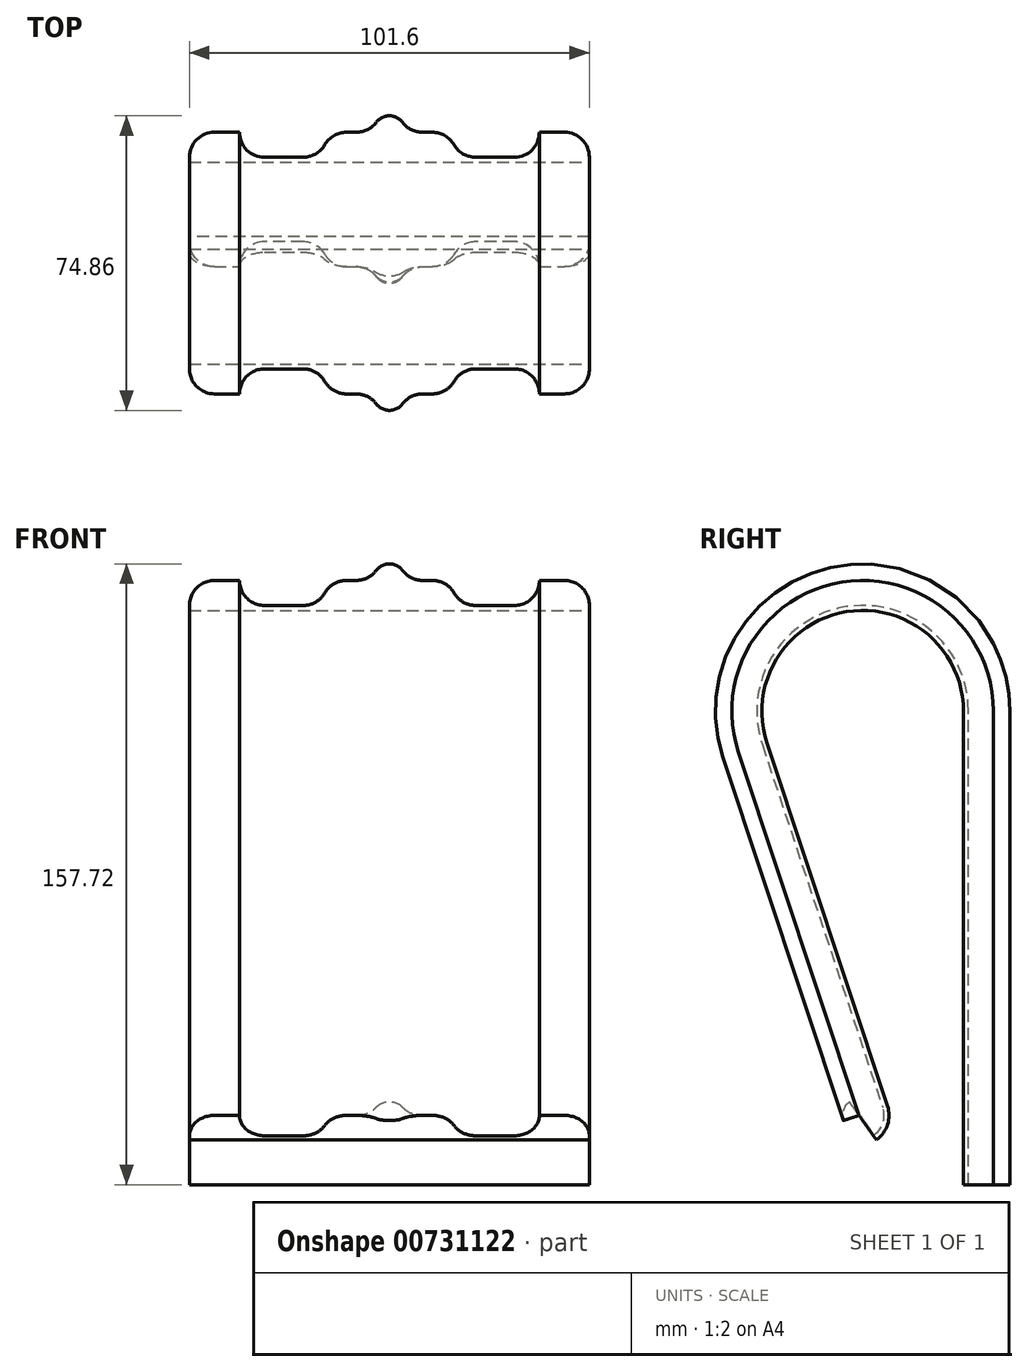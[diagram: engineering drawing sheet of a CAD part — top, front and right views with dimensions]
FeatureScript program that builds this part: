
annotation { "Feature Type Name" : "Feature", "Feature Type Description" : "" }
export const myFeature = defineFeature(function(context is Context, id is Id, definition is map)
    precondition{}
    {
        {
            var Q0;
            Q0=qCreatedBy(makeId("Front.planeOp"),FACE);
            var sketch = newSketch(context, id + "F0", { "sketchPlane" : qUnion([Q0])});
            skLineSegment(sketch, "E0.bottom", {"start": v(-50.8, 0) * mm, "end": v(50.8, 0) * mm});
            skLineSegment(sketch, "E0.top", {"start": v(-44.45, 7.62) * mm, "end": v(-38.1, 7.62) * mm});
            skLineSegment(sketch, "E0.left", {"start": v(-50.8, 0) * mm, "end": v(-50.8, 1.27) * mm});
            skLineSegment(sketch, "E0.right", {"start": v(50.8, 0) * mm, "end": v(50.8, 1.27) * mm});
            skLineSegment(sketch, "E1", {"start": v(-38.1, 7.62) * mm, "end": v(-38.1, 7.62) * mm});
            skLineSegment(sketch, "E2", {"start": v(-31.75, 1.27) * mm, "end": v(-21.93, 1.27) * mm});
            skLineSegment(sketch, "E3", {"start": v(-15.58, 7.62) * mm, "end": v(-15.58, 7.62) * mm});
            skArc(sketch, "E4", {"start": v(3.35, 10.15) * mm, "mid": v(0, 11.82) * mm, "end": v(-3.35, 10.15) * mm});
            skLineSegment(sketch, "E5", {"start": v(15.58, 7.62) * mm, "end": v(15.58, 7.62) * mm});
            skLineSegment(sketch, "E6", {"start": v(21.93, 1.27) * mm, "end": v(31.75, 1.27) * mm});
            skLineSegment(sketch, "E7", {"start": v(38.1, 7.62) * mm, "end": v(38.1, 7.62) * mm});
            skPoint(sketch, "E8.visualSharp", {"position": v(-50.8, 7.62) * mm});
            skArc(sketch, "E8.filletArc", {"start": v(-44.45, 7.62) * mm, "mid": v(-48.94, 5.76) * mm, "end": v(-50.8, 1.27) * mm});
            skPoint(sketch, "E9.visualSharp", {"position": v(-38.1, 1.27) * mm});
            skArc(sketch, "E9.filletArc", {"start": v(-38.1, 7.62) * mm, "mid": v(-36.24, 3.13) * mm, "end": v(-31.75, 1.27) * mm});
            skPoint(sketch, "E10.visualSharp", {"position": v(-15.58, 1.27) * mm});
            skArc(sketch, "E10.filletArc", {"start": v(-21.93, 1.27) * mm, "mid": v(-18.75, 2.12) * mm, "end": v(-16.43, 4.45) * mm});
            skPoint(sketch, "E11.visualSharp", {"position": v(15.58, 1.27) * mm});
            skArc(sketch, "E11.filletArc", {"start": v(16.43, 4.44) * mm, "mid": v(18.75, 2.12) * mm, "end": v(21.93, 1.27) * mm});
            skPoint(sketch, "E12.visualSharp", {"position": v(38.1, 1.27) * mm});
            skArc(sketch, "E12.filletArc", {"start": v(31.75, 1.27) * mm, "mid": v(36.24, 3.13) * mm, "end": v(38.1, 7.62) * mm});
            skPoint(sketch, "E13.visualSharp", {"position": v(50.8, 7.62) * mm});
            skArc(sketch, "E13.filletArc", {"start": v(50.8, 1.27) * mm, "mid": v(48.94, 5.76) * mm, "end": v(44.45, 7.62) * mm});
            skLineSegment(sketch, "E14", {"start": v(-38.1, 7.62) * mm, "end": v(-15.58, 7.62) * mm});
            skLineSegment(sketch, "E15", {"start": v(-10.93, 7.62) * mm, "end": v(-8.42, 7.62) * mm});
            skLineSegment(sketch, "E16", {"start": v(15.58, 7.62) * mm, "end": v(38.1, 7.62) * mm});
            skLineSegment(sketch, "E17", {"start": v(38.1, 7.62) * mm, "end": v(44.45, 7.62) * mm});
            skPoint(sketch, "E18.visualSharp", {"position": v(-15.58, 7.62) * mm});
            skArc(sketch, "E18.filletArc", {"start": v(-10.93, 7.62) * mm, "mid": v(-14.1, 6.77) * mm, "end": v(-16.43, 4.44) * mm});
            skPoint(sketch, "E19.visualSharp", {"position": v(15.58, 7.62) * mm});
            skArc(sketch, "E19.filletArc", {"start": v(16.43, 4.44) * mm, "mid": v(14.1, 6.77) * mm, "end": v(10.93, 7.62) * mm});
            skLineSegment(sketch, "E20", {"start": v(-4.2, 7.62) * mm, "end": v(3.36, 7.62) * mm});
            skLineSegment(sketch, "E21", {"start": v(8.42, 7.62) * mm, "end": v(10.93, 7.62) * mm});
            skPoint(sketch, "E22.visualSharp", {"position": v(-4.2, 7.62) * mm});
            skArc(sketch, "E22.filletArc", {"start": v(-8.42, 7.62) * mm, "mid": v(-5.6, 8.29) * mm, "end": v(-3.35, 10.15) * mm});
            skPoint(sketch, "E23.newPointB", {"position": v(3.36, 7.62) * mm});
            skArc(sketch, "E23.filletArc", {"start": v(3.35, 10.15) * mm, "mid": v(5.6, 8.29) * mm, "end": v(8.42, 7.62) * mm});
            skSolve(sketch);
        }
        {
            var Q0;
            Q0=qCreatedBy(makeId("Right.planeOp"),FACE);
            var sketch = newSketch(context, id + "F1", { "sketchPlane" : qUnion([Q0])});
            skArc(sketch, "E24", {"start": v(26.88, -25.6) * mm, "mid": v(-4.29, 0.93) * mm, "end": v(-25.5, -34.08) * mm});
            skPoint(sketch, "E25.0", {"position": v(0, 1.27) * mm});
            skArc(sketch, "E26", {"start": v(2.76, -133.47) * mm, "mid": v(4.62, -159.47) * mm, "end": v(26.88, -145.9) * mm});
            skPoint(sketch, "E27", {"position": v(26.88, -145.9) * mm});
            skPoint(sketch, "E28", {"position": v(26.88, -25.6) * mm});
            skLineSegment(sketch, "E29", {"start": v(26.88, -25.6) * mm, "end": v(26.88, -145.9) * mm});
            skLineSegment(sketch, "E30", {"start": v(5.1, -126.3) * mm, "end": v(-25.5, -34.08) * mm});
            skPoint(sketch, "E31.visualSharp", {"position": v(6.8, -131.42) * mm});
            skArc(sketch, "E31.filletArc", {"start": v(2.76, -133.47) * mm, "mid": v(5.12, -130.27) * mm, "end": v(5.1, -126.3) * mm});
            skSolve(sketch);
        }
        {
            var Q0;
            Q0=makeQuery(id+"F0.imprint","IMPRINT",FACE,{"disambiguationData":[TD([[makeQuery(id+"F0.imprint","IMPRINT",EDGE,{"derivedFrom":sQuery(id+"F0.wireOp",EDGE,"E0.bottom")}),1.0]])]});
            var Q1;
            Q1=sQuery(id+"F1.wireOp",EDGE,"E24");
            var Q2;
            Q2=sQuery(id+"F1.wireOp",EDGE,"E30");
            var Q3;
            Q3=sQuery(id+"F1.wireOp",EDGE,"E29");
            var Q4;
            Q4=sQuery(id+"F1.wireOp",EDGE,"E31.filletArc");
            sweep(context, id + "F2", {"profiles" : qUnion([Q0]), "path" : qUnion([Q1, Q2, Q3, Q4])});
        }
    });
